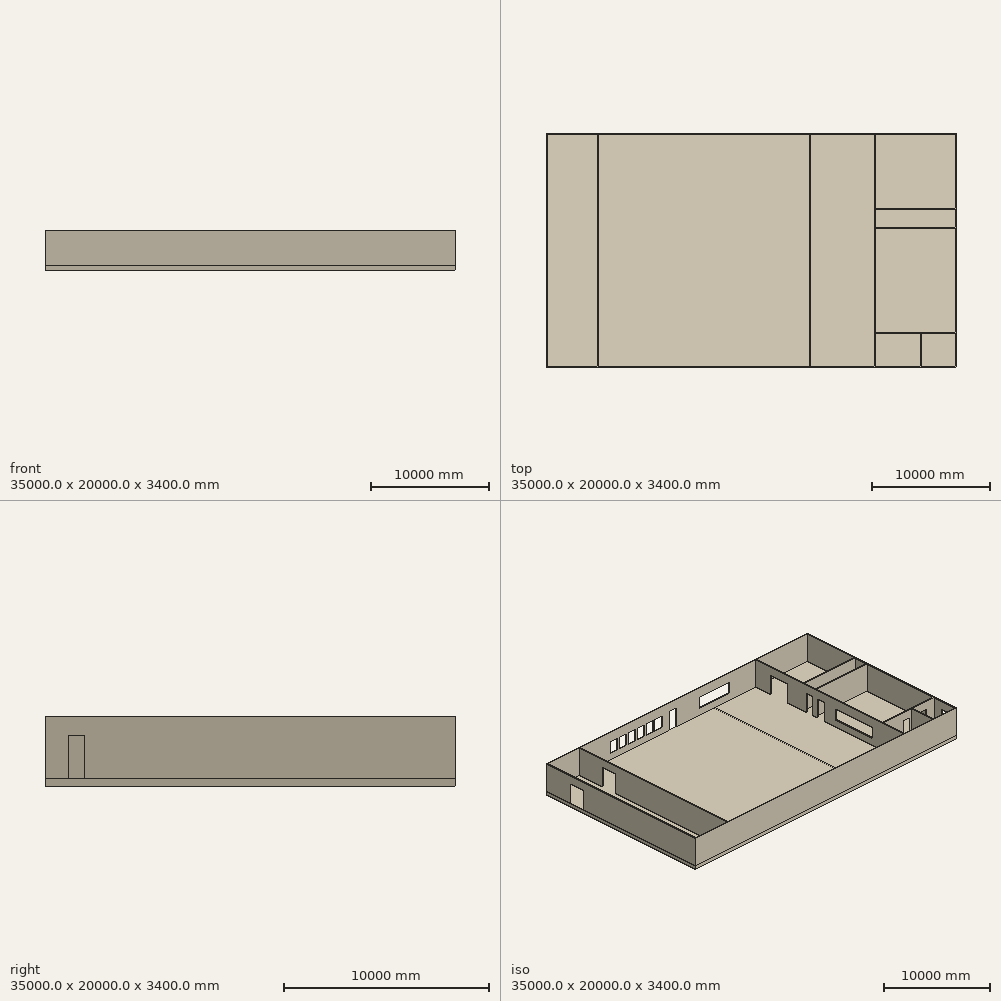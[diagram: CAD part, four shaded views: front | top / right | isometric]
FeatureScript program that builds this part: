
annotation { "Feature Type Name" : "Feature", "Feature Type Description" : "" }
export const myFeature = defineFeature(function(context is Context, id is Id, definition is map)
    precondition{}
    {
        {
            var Q0;
            Q0=qCreatedBy(makeId("Top.planeOp"),FACE);
            var sketch = newSketch(context, id + "F0", { "sketchPlane" : qUnion([Q0])});
            skLineSegment(sketch, "E0.bottom", {"start": v(0, 0) * mm, "end": v(-35000, 0) * mm});
            skLineSegment(sketch, "E0.right", {"start": v(-35000, 0) * mm, "end": v(-35000, 20000) * mm});
            skLineSegment(sketch, "E1.0", {"start": v(-34900, 100) * mm, "end": v(-34900, 19900) * mm});
            skLineSegment(sketch, "E2", {"start": v(-3000, 100) * mm, "end": v(-3000, 2905) * mm});
            skLineSegment(sketch, "E3", {"start": v(-3000, 2905) * mm, "end": v(-1985, 2905) * mm});
            skPoint(sketch, "E4", {"position": v(-100, 2905) * mm});
            skLineSegment(sketch, "E5", {"start": v(-1115, 2905) * mm, "end": v(-100, 2905) * mm});
            skLineSegment(sketch, "E6", {"start": v(-1985, 2905) * mm, "end": v(-1985, 3005) * mm});
            skLineSegment(sketch, "E7", {"start": v(-1115, 2905) * mm, "end": v(-1115, 3005) * mm});
            skLineSegment(sketch, "E8", {"start": v(-1115, 3005) * mm, "end": v(-100, 3005) * mm});
            skLineSegment(sketch, "E9", {"start": v(-3000, 100) * mm, "end": v(-100, 100) * mm});
            skLineSegment(sketch, "E10", {"start": v(-100, 2905) * mm, "end": v(-100, 1890) * mm});
            skLineSegment(sketch, "E11", {"start": v(-100, 100) * mm, "end": v(-100, 1115) * mm});
            skLineSegment(sketch, "E12", {"start": v(-100, 1115) * mm, "end": v(0, 1115) * mm});
            skLineSegment(sketch, "E13", {"start": v(0, 1115) * mm, "end": v(0, 0) * mm});
            skLineSegment(sketch, "E14", {"start": v(-100, 1890) * mm, "end": v(0, 1890) * mm});
            skLineSegment(sketch, "E15", {"start": v(0, 1890) * mm, "end": v(0, 20000) * mm});
            skLineSegment(sketch, "E16", {"start": v(0, 1890) * mm, "end": v(0, 1115) * mm});
            skLineSegment(sketch, "E17", {"start": v(-100, 11905) * mm, "end": v(-6900, 11905) * mm});
            skLineSegment(sketch, "E18", {"start": v(-6900, 12005) * mm, "end": v(-100, 12005) * mm});
            skLineSegment(sketch, "E19", {"start": v(-100, 3005) * mm, "end": v(-100, 11905) * mm});
            skLineSegment(sketch, "E20", {"start": v(-6900, 11905) * mm, "end": v(-6900, 11655) * mm});
            skLineSegment(sketch, "E21", {"start": v(-6900, 11655) * mm, "end": v(-7000, 11655) * mm});
            skLineSegment(sketch, "E22", {"start": v(-7000, 11655) * mm, "end": v(-7000, 12255) * mm});
            skLineSegment(sketch, "E23", {"start": v(-7000, 12255) * mm, "end": v(-6900, 12255) * mm});
            skLineSegment(sketch, "E24", {"start": v(-6900, 12255) * mm, "end": v(-6900, 12005) * mm});
            skLineSegment(sketch, "E25", {"start": v(-6900, 13125) * mm, "end": v(-7000, 13125) * mm});
            skLineSegment(sketch, "E26", {"start": v(-6900, 19900) * mm, "end": v(-95.24, 19900) * mm});
            skLineSegment(sketch, "E27", {"start": v(-3100, 100) * mm, "end": v(-6900, 100) * mm});
            skLineSegment(sketch, "E28", {"start": v(-7000, 100) * mm, "end": v(-7000, 10755) * mm});
            skLineSegment(sketch, "E29", {"start": v(-7000, 10755) * mm, "end": v(-6900, 10755) * mm});
            skLineSegment(sketch, "E30", {"start": v(-1985, 2905) * mm, "end": v(-1115, 2905) * mm});
            skLineSegment(sketch, "E31", {"start": v(-1985, 3005) * mm, "end": v(-1115, 3005) * mm});
            skLineSegment(sketch, "E32", {"start": v(-6900, 10755) * mm, "end": v(-6900, 11655) * mm});
            skLineSegment(sketch, "E33", {"start": v(-7000, 11655) * mm, "end": v(-7000, 10755) * mm});
            skLineSegment(sketch, "E34", {"start": v(-7000, 12255) * mm, "end": v(-7000, 13125) * mm});
            skLineSegment(sketch, "E35", {"start": v(-6900, 12255) * mm, "end": v(-6900, 13125) * mm});
            skLineSegment(sketch, "E36", {"start": v(-100, 1890) * mm, "end": v(-100, 1115) * mm});
            skLineSegment(sketch, "E37", {"start": v(-7000, 9255) * mm, "end": v(-6900, 9255) * mm});
            skLineSegment(sketch, "E38", {"start": v(-7000, 4255) * mm, "end": v(-6900, 4255) * mm});
            skLineSegment(sketch, "E39", {"start": v(-3100, 100) * mm, "end": v(-3100, 2905) * mm});
            skLineSegment(sketch, "E40", {"start": v(-6900, 100) * mm, "end": v(-6900, 2905) * mm});
            skLineSegment(sketch, "E41", {"start": v(-6900, 3005) * mm, "end": v(-6900, 9255) * mm});
            skLineSegment(sketch, "E42", {"start": v(-6900, 10755) * mm, "end": v(-6900, 9255) * mm});
            skLineSegment(sketch, "E43", {"start": v(-3100, 2905) * mm, "end": v(-3350, 2905) * mm});
            skLineSegment(sketch, "E44", {"start": v(-3350, 2905) * mm, "end": v(-4220, 2905) * mm});
            skLineSegment(sketch, "E45", {"start": v(-6900, 2905) * mm, "end": v(-4220, 2905) * mm});
            skLineSegment(sketch, "E46", {"start": v(-1985, 3005) * mm, "end": v(-3350, 3005) * mm});
            skLineSegment(sketch, "E47", {"start": v(-3350, 3005) * mm, "end": v(-4220, 3005) * mm});
            skLineSegment(sketch, "E48", {"start": v(-4220, 3005) * mm, "end": v(-6900, 3005) * mm});
            skLineSegment(sketch, "E49", {"start": v(-3350, 3005) * mm, "end": v(-3350, 2905) * mm});
            skLineSegment(sketch, "E50", {"start": v(-4220, 3005) * mm, "end": v(-4220, 2905) * mm});
            skLineSegment(sketch, "E51", {"start": v(-6900, 13505) * mm, "end": v(-100, 13505) * mm});
            skLineSegment(sketch, "E52", {"start": v(-6900, 13125) * mm, "end": v(-6900, 13505) * mm});
            skLineSegment(sketch, "E53", {"start": v(-100, 12005) * mm, "end": v(-100, 13505) * mm});
            skLineSegment(sketch, "E54", {"start": v(-95.24, 19900) * mm, "end": v(-95.24, 13605) * mm});
            skLineSegment(sketch, "E55", {"start": v(-95.24, 13605) * mm, "end": v(-6900, 13605) * mm});
            skLineSegment(sketch, "E56", {"start": v(-6900, 19900) * mm, "end": v(-6900, 17900) * mm});
            skLineSegment(sketch, "E57", {"start": v(-6900, 13605) * mm, "end": v(-6900, 15605) * mm});
            skLineSegment(sketch, "E58", {"start": v(-7000, 19900) * mm, "end": v(-7000, 17900) * mm});
            skLineSegment(sketch, "E59", {"start": v(-7000, 15605) * mm, "end": v(-7000, 13125) * mm});
            skLineSegment(sketch, "E60", {"start": v(-7000, 17900) * mm, "end": v(-6900, 17900) * mm});
            skLineSegment(sketch, "E61", {"start": v(-7000, 17900) * mm, "end": v(-7000, 15605) * mm});
            skLineSegment(sketch, "E62", {"start": v(-6900, 17900) * mm, "end": v(-6900, 15605) * mm});
            skLineSegment(sketch, "E63", {"start": v(-7000, 15605) * mm, "end": v(-6900, 15605) * mm});
            skLineSegment(sketch, "E64", {"start": v(-7000, 100) * mm, "end": v(-12500, 100) * mm});
            skLineSegment(sketch, "E65", {"start": v(-12500, 100) * mm, "end": v(-12500, 19900) * mm});
            skLineSegment(sketch, "E66", {"start": v(-12500, 19900) * mm, "end": v(-12550, 19900) * mm});
            skLineSegment(sketch, "E67", {"start": v(-12550, 19900) * mm, "end": v(-12550, 100) * mm});
            skLineSegment(sketch, "E68", {"start": v(-12500, 100) * mm, "end": v(-12550, 100) * mm});
            skLineSegment(sketch, "E69", {"start": v(-12550, 100) * mm, "end": v(-30550, 100) * mm});
            skLineSegment(sketch, "E70", {"start": v(-30550, 100) * mm, "end": v(-30550, 15100) * mm});
            skLineSegment(sketch, "E71", {"start": v(-30550, 15100) * mm, "end": v(-30550, 16840) * mm});
            skLineSegment(sketch, "E72", {"start": v(-30550, 16840) * mm, "end": v(-30550, 19900) * mm});
            skLineSegment(sketch, "E73", {"start": v(-7000, 19900) * mm, "end": v(-12500, 19900) * mm});
            skLineSegment(sketch, "E74", {"start": v(-34900, 100) * mm, "end": v(-30650, 100) * mm});
            skLineSegment(sketch, "E75", {"start": v(-30650, 100) * mm, "end": v(-30650, 15100) * mm});
            skLineSegment(sketch, "E76", {"start": v(-30650, 15100) * mm, "end": v(-30650, 16840) * mm});
            skLineSegment(sketch, "E77", {"start": v(-30650, 16840) * mm, "end": v(-30650, 19900) * mm});
            skLineSegment(sketch, "E78", {"start": v(-30650, 19900) * mm, "end": v(-34900, 19900) * mm});
            skLineSegment(sketch, "E79", {"start": v(-30650, 15100) * mm, "end": v(-30550, 15100) * mm});
            skLineSegment(sketch, "E80", {"start": v(-30650, 16840) * mm, "end": v(-30550, 16840) * mm});
            skLineSegment(sketch, "E81", {"start": v(-30550, 19900) * mm, "end": v(-26550, 19900) * mm});
            skLineSegment(sketch, "E82", {"start": v(-26550, 19900) * mm, "end": v(-25550, 19900) * mm});
            skLineSegment(sketch, "E83", {"start": v(-25550, 19900) * mm, "end": v(-25350, 19900) * mm});
            skLineSegment(sketch, "E84", {"start": v(-25350, 19900) * mm, "end": v(-24350, 19900) * mm});
            skLineSegment(sketch, "E85", {"start": v(-24350, 19900) * mm, "end": v(-24150, 19900) * mm});
            skLineSegment(sketch, "E86", {"start": v(-24150, 19900) * mm, "end": v(-23150, 19900) * mm});
            skLineSegment(sketch, "E87", {"start": v(-23150, 19900) * mm, "end": v(-22950, 19900) * mm});
            skLineSegment(sketch, "E88", {"start": v(-22950, 19900) * mm, "end": v(-21950, 19900) * mm});
            skLineSegment(sketch, "E89", {"start": v(-21950, 19900) * mm, "end": v(-21750, 19900) * mm});
            skLineSegment(sketch, "E90", {"start": v(-21750, 19900) * mm, "end": v(-20750, 19900) * mm});
            skLineSegment(sketch, "E91", {"start": v(-20750, 19900) * mm, "end": v(-20550, 19900) * mm});
            skLineSegment(sketch, "E92", {"start": v(-20550, 19900) * mm, "end": v(-19550, 19900) * mm});
            skLineSegment(sketch, "E93", {"start": v(-26550, 19900) * mm, "end": v(-26550, 20000) * mm});
            skLineSegment(sketch, "E94", {"start": v(-25550, 19900) * mm, "end": v(-25550, 20000) * mm});
            skLineSegment(sketch, "E95", {"start": v(-25350, 19900) * mm, "end": v(-25350, 20000) * mm});
            skLineSegment(sketch, "E96", {"start": v(-24350, 19900) * mm, "end": v(-24350, 20000) * mm});
            skLineSegment(sketch, "E97", {"start": v(-24150, 19900) * mm, "end": v(-24150, 20000) * mm});
            skLineSegment(sketch, "E98", {"start": v(-23150, 19900) * mm, "end": v(-23150, 20000) * mm});
            skLineSegment(sketch, "E99", {"start": v(-22950, 19900) * mm, "end": v(-22950, 20000) * mm});
            skLineSegment(sketch, "E100", {"start": v(-21950, 19900) * mm, "end": v(-21950, 20000) * mm});
            skLineSegment(sketch, "E101", {"start": v(-20750, 19900) * mm, "end": v(-20750, 20000) * mm});
            skLineSegment(sketch, "E102", {"start": v(-20550, 19900) * mm, "end": v(-20550, 20000) * mm});
            skLineSegment(sketch, "E103", {"start": v(-19550, 19900) * mm, "end": v(-19550, 20000) * mm});
            skLineSegment(sketch, "E104", {"start": v(-21750, 19900) * mm, "end": v(-21750, 20000) * mm});
            skLineSegment(sketch, "E105", {"start": v(-19550, 19900) * mm, "end": v(-18550, 19900) * mm});
            skLineSegment(sketch, "E106", {"start": v(-18550, 19900) * mm, "end": v(-17680, 19900) * mm});
            skLineSegment(sketch, "E107", {"start": v(-12550, 19900) * mm, "end": v(-17680, 19900) * mm});
            skLineSegment(sketch, "E108", {"start": v(-18550, 19900) * mm, "end": v(-18550, 20000) * mm});
            skLineSegment(sketch, "E109", {"start": v(-17680, 19900) * mm, "end": v(-17680, 20000) * mm});
            skLineSegment(sketch, "E110", {"start": v(0, 20000) * mm, "end": v(-17680, 20000) * mm});
            skLineSegment(sketch, "E111", {"start": v(-17680, 20000) * mm, "end": v(-18550, 20000) * mm});
            skLineSegment(sketch, "E112", {"start": v(-18550, 20000) * mm, "end": v(-19550, 20000) * mm});
            skLineSegment(sketch, "E113", {"start": v(-19550, 20000) * mm, "end": v(-20550, 20000) * mm});
            skLineSegment(sketch, "E114", {"start": v(-20550, 20000) * mm, "end": v(-20750, 20000) * mm});
            skLineSegment(sketch, "E115", {"start": v(-20750, 20000) * mm, "end": v(-21750, 20000) * mm});
            skLineSegment(sketch, "E116", {"start": v(-21750, 20000) * mm, "end": v(-21950, 20000) * mm});
            skLineSegment(sketch, "E117", {"start": v(-21950, 20000) * mm, "end": v(-22950, 20000) * mm});
            skLineSegment(sketch, "E118", {"start": v(-22950, 20000) * mm, "end": v(-23150, 20000) * mm});
            skLineSegment(sketch, "E119", {"start": v(-23150, 20000) * mm, "end": v(-24150, 20000) * mm});
            skLineSegment(sketch, "E120", {"start": v(-24150, 20000) * mm, "end": v(-24350, 20000) * mm});
            skLineSegment(sketch, "E121", {"start": v(-24350, 20000) * mm, "end": v(-25350, 20000) * mm});
            skLineSegment(sketch, "E122", {"start": v(-25350, 20000) * mm, "end": v(-25550, 20000) * mm});
            skLineSegment(sketch, "E123", {"start": v(-25550, 20000) * mm, "end": v(-26550, 20000) * mm});
            skLineSegment(sketch, "E124", {"start": v(-26550, 20000) * mm, "end": v(-35000, 20000) * mm});
            skLineSegment(sketch, "E125", {"start": v(-35000, 15100) * mm, "end": v(-34900, 15100) * mm});
            skLineSegment(sketch, "E126", {"start": v(-35000, 16840) * mm, "end": v(-34900, 16840) * mm});
            skLineSegment(sketch, "E127", {"start": v(-14600, 20000) * mm, "end": v(-14600, 19900) * mm});
            skLineSegment(sketch, "E128", {"start": v(-10600, 20000) * mm, "end": v(-10600, 19900) * mm});
            skSolve(sketch);
        }
        {
            var Q0;
            Q0=makeQuery(id+"F0.imprint","IMPRINT",FACE,{"disambiguationData":[TD([[makeQuery(id+"F0.imprint","IMPRINT",EDGE,{"derivedFrom":sQuery(id+"F0.wireOp",EDGE,"E1.0")}),-1.0]])]});
            var Q1;
            Q1=makeQuery(id+"F0.imprint","IMPRINT",FACE,{"disambiguationData":[TD([[makeQuery(id+"F0.imprint","IMPRINT",EDGE,{"derivedFrom":sQuery(id+"F0.wireOp",EDGE,"E0.bottom")}),-1.0]])]});
            var Q2;
            Q2=makeQuery(id+"F0.imprint","IMPRINT",FACE,{"disambiguationData":[TD([[makeQuery(id+"F0.imprint","IMPRINT",EDGE,{"derivedFrom":sQuery(id+"F0.wireOp",EDGE,"E2")}),-1.0]])]});
            var Q3;
            Q3=makeQuery(id+"F0.imprint","IMPRINT",FACE,{"disambiguationData":[TD([[makeQuery(id+"F0.imprint","IMPRINT",EDGE,{"derivedFrom":sQuery(id+"F0.wireOp",EDGE,"E12")}),1.0]])]});
            var Q4;
            Q4=makeQuery(id+"F0.imprint","IMPRINT",FACE,{"disambiguationData":[TD([[makeQuery(id+"F0.imprint","IMPRINT",EDGE,{"derivedFrom":sQuery(id+"F0.wireOp",EDGE,"E6")}),-1.0]])]});
            var Q5;
            Q5=makeQuery(id+"F0.imprint","IMPRINT",FACE,{"disambiguationData":[TD([[makeQuery(id+"F0.imprint","IMPRINT",EDGE,{"derivedFrom":sQuery(id+"F0.wireOp",EDGE,"6b3fb178-0d36-4cbd-b119-71aa7d92e045.4")}),1.0]])]});
            var Q6;
            Q6=makeQuery(id+"F0.imprint","IMPRINT",FACE,{"disambiguationData":[TD([[makeQuery(id+"F0.imprint","IMPRINT",EDGE,{"derivedFrom":sQuery(id+"F0.wireOp",EDGE,"E21")}),1.0]])]});
            var Q7;
            Q7=makeQuery(id+"F0.imprint","IMPRINT",FACE,{"disambiguationData":[TD([[makeQuery(id+"F0.imprint","IMPRINT",EDGE,{"derivedFrom":sQuery(id+"F0.wireOp",EDGE,"E18")}),1.0]])]});
            var Q8;
            Q8=makeQuery(id+"F0.imprint","IMPRINT",FACE,{"disambiguationData":[TD([[makeQuery(id+"F0.imprint","IMPRINT",EDGE,{"derivedFrom":sQuery(id+"F0.wireOp",EDGE,"E23")}),1.0]])]});
            var Q9;
            {var subQ0=sQuery(id+"F0.wireOp",EDGE,"E37");Q9=makeQuery(id+"F0.imprint","IMPRINT",FACE,{"disambiguationData":[TD([[makeQuery(id+"F0.imprint","IMPRINT",EDGE,{"derivedFrom":subQ0}),-1.0]])]});}
            var Q10;
            {var subQ0=sQuery(id+"F0.wireOp",EDGE,"E29");Q10=makeQuery(id+"F0.imprint","IMPRINT",FACE,{"disambiguationData":[TD([[makeQuery(id+"F0.imprint","IMPRINT",EDGE,{"derivedFrom":subQ0}),-1.0]])]});}
            var Q11;
            {var subQ5=sQuery(id+"F0.wireOp",EDGE,"KWLxwDUW-hbxq-1viL-1m08-Hg8gEenvGZlB");Q11=makeQuery(id+"F0.imprint","IMPRINT",FACE,{"disambiguationData":[TD([[makeQuery(id+"F0.imprint","IMPRINT",EDGE,{"derivedFrom":subQ5}),-1.0]])]});}
            var Q12;
            {var subQ0=sQuery(id+"F0.wireOp",EDGE,"sINUJQdt-DprZ-GAcK-VXLo-GtyemsUMvXYI");Q12=makeQuery(id+"F0.imprint","IMPRINT",FACE,{"disambiguationData":[TD([[makeQuery(id+"F0.imprint","IMPRINT",EDGE,{"derivedFrom":subQ0}),-1.0]])]});}
            var Q13;
            Q13=makeQuery(id+"F0.imprint","IMPRINT",FACE,{"disambiguationData":[TD([[makeQuery(id+"F0.imprint","IMPRINT",EDGE,{"derivedFrom":sQuery(id+"F0.wireOp",EDGE,"E27")}),-1.0]])]});
            var Q14;
            Q14=makeQuery(id+"F0.imprint","IMPRINT",FACE,{"disambiguationData":[TD([[makeQuery(id+"F0.imprint","IMPRINT",EDGE,{"derivedFrom":sQuery(id+"F0.wireOp",EDGE,"E8")}),1.0]])]});
            var Q15;
            Q15=makeQuery(id+"F0.imprint","IMPRINT",FACE,{"disambiguationData":[TD([[makeQuery(id+"F0.imprint","IMPRINT",EDGE,{"derivedFrom":sQuery(id+"F0.wireOp",EDGE,"E44")}),-1.0]])]});
            var Q16;
            Q16=makeQuery(id+"F0.imprint","IMPRINT",FACE,{"disambiguationData":[TD([[makeQuery(id+"F0.imprint","IMPRINT",EDGE,{"derivedFrom":sQuery(id+"F0.wireOp",EDGE,"E26")}),-1.0]])]});
            var Q17;
            Q17=makeQuery(id+"F0.imprint","IMPRINT",FACE,{"disambiguationData":[TD([[makeQuery(id+"F0.imprint","IMPRINT",EDGE,{"derivedFrom":sQuery(id+"F0.wireOp",EDGE,"E60")}),-1.0]])]});
            var Q18;
            Q18=makeQuery(id+"F0.imprint","IMPRINT",FACE,{"disambiguationData":[TD([[makeQuery(id+"F0.imprint","IMPRINT",EDGE,{"derivedFrom":sQuery(id+"F0.wireOp",EDGE,"E67")}),-1.0]])]});
            var Q19;
            Q19=makeQuery(id+"F0.imprint","IMPRINT",FACE,{"disambiguationData":[TD([[makeQuery(id+"F0.imprint","IMPRINT",EDGE,{"derivedFrom":sQuery(id+"F0.wireOp",EDGE,"E22")}),1.0]])]});
            var Q20;
            Q20=makeQuery(id+"F0.imprint","IMPRINT",FACE,{"disambiguationData":[TD([[makeQuery(id+"F0.imprint","IMPRINT",EDGE,{"derivedFrom":sQuery(id+"F0.wireOp",EDGE,"E65")}),1.0]])]});
            var Q21;
            Q21=makeQuery(id+"F0.imprint","IMPRINT",FACE,{"disambiguationData":[TD([[makeQuery(id+"F0.imprint","IMPRINT",EDGE,{"derivedFrom":sQuery(id+"F0.wireOp",EDGE,"E71")}),1.0]])]});
            var Q22;
            Q22=makeQuery(id+"F0.imprint","IMPRINT",FACE,{"disambiguationData":[TD([[makeQuery(id+"F0.imprint","IMPRINT",EDGE,{"derivedFrom":sQuery(id+"F0.wireOp",EDGE,"E82")}),1.0]])]});
            var Q23;
            Q23=makeQuery(id+"F0.imprint","IMPRINT",FACE,{"disambiguationData":[TD([[makeQuery(id+"F0.imprint","IMPRINT",EDGE,{"derivedFrom":sQuery(id+"F0.wireOp",EDGE,"E83")}),1.0]])]});
            var Q24;
            Q24=makeQuery(id+"F0.imprint","IMPRINT",FACE,{"disambiguationData":[TD([[makeQuery(id+"F0.imprint","IMPRINT",EDGE,{"derivedFrom":sQuery(id+"F0.wireOp",EDGE,"E84")}),1.0]])]});
            var Q25;
            Q25=makeQuery(id+"F0.imprint","IMPRINT",FACE,{"disambiguationData":[TD([[makeQuery(id+"F0.imprint","IMPRINT",EDGE,{"derivedFrom":sQuery(id+"F0.wireOp",EDGE,"E85")}),1.0]])]});
            var Q26;
            Q26=makeQuery(id+"F0.imprint","IMPRINT",FACE,{"disambiguationData":[TD([[makeQuery(id+"F0.imprint","IMPRINT",EDGE,{"derivedFrom":sQuery(id+"F0.wireOp",EDGE,"E86")}),1.0]])]});
            var Q27;
            Q27=makeQuery(id+"F0.imprint","IMPRINT",FACE,{"disambiguationData":[TD([[makeQuery(id+"F0.imprint","IMPRINT",EDGE,{"derivedFrom":sQuery(id+"F0.wireOp",EDGE,"E87")}),1.0]])]});
            var Q28;
            Q28=makeQuery(id+"F0.imprint","IMPRINT",FACE,{"disambiguationData":[TD([[makeQuery(id+"F0.imprint","IMPRINT",EDGE,{"derivedFrom":sQuery(id+"F0.wireOp",EDGE,"E88")}),1.0]])]});
            var Q29;
            Q29=makeQuery(id+"F0.imprint","IMPRINT",FACE,{"disambiguationData":[TD([[makeQuery(id+"F0.imprint","IMPRINT",EDGE,{"derivedFrom":sQuery(id+"F0.wireOp",EDGE,"E89")}),1.0]])]});
            var Q30;
            Q30=makeQuery(id+"F0.imprint","IMPRINT",FACE,{"disambiguationData":[TD([[makeQuery(id+"F0.imprint","IMPRINT",EDGE,{"derivedFrom":sQuery(id+"F0.wireOp",EDGE,"E90")}),1.0]])]});
            var Q31;
            Q31=makeQuery(id+"F0.imprint","IMPRINT",FACE,{"disambiguationData":[TD([[makeQuery(id+"F0.imprint","IMPRINT",EDGE,{"derivedFrom":sQuery(id+"F0.wireOp",EDGE,"E91")}),1.0]])]});
            var Q32;
            Q32=makeQuery(id+"F0.imprint","IMPRINT",FACE,{"disambiguationData":[TD([[makeQuery(id+"F0.imprint","IMPRINT",EDGE,{"derivedFrom":sQuery(id+"F0.wireOp",EDGE,"E92")}),1.0]])]});
            var Q33;
            Q33=makeQuery(id+"F0.imprint","IMPRINT",FACE,{"disambiguationData":[TD([[makeQuery(id+"F0.imprint","IMPRINT",EDGE,{"derivedFrom":sQuery(id+"F0.wireOp",EDGE,"E103")}),-1.0]])]});
            var Q34;
            Q34=makeQuery(id+"F0.imprint","IMPRINT",FACE,{"disambiguationData":[TD([[makeQuery(id+"F0.imprint","IMPRINT",EDGE,{"derivedFrom":sQuery(id+"F0.wireOp",EDGE,"E106")}),1.0]])]});
            var Q35;
            Q35=makeQuery(id+"F0.imprint","IMPRINT",FACE,{"disambiguationData":[TD([[makeQuery(id+"F0.imprint","IMPRINT",EDGE,{"derivedFrom":sQuery(id+"F0.wireOp",EDGE,"E5")}),1.0]])]});
            var Q36;
            Q36=makeQuery(id+"F0.imprint","IMPRINT",FACE,{"disambiguationData":[TD([[makeQuery(id+"F0.imprint","IMPRINT",EDGE,{"derivedFrom":sQuery(id+"F0.wireOp",EDGE,"E72")}),1.0]])]});
            var Q37;
            {var subQ0=sQuery(id+"F0.wireOp",EDGE,"E125");Q37=makeQuery(id+"F0.imprint","IMPRINT",FACE,{"disambiguationData":[TD([[makeQuery(id+"F0.imprint","IMPRINT",EDGE,{"derivedFrom":subQ0}),1.0]])]});}
            var Q38;
            {var subQ4=sQuery(id+"F0.wireOp",EDGE,"E66");Q38=makeQuery(id+"F0.imprint","IMPRINT",FACE,{"disambiguationData":[TD([[makeQuery(id+"F0.imprint","IMPRINT",EDGE,{"derivedFrom":subQ4}),-1.0]])]});}
            var Q39;
            {var subQ0=sQuery(id+"F0.wireOp",EDGE,"E109");Q39=makeQuery(id+"F0.imprint","IMPRINT",FACE,{"disambiguationData":[TD([[makeQuery(id+"F0.imprint","IMPRINT",EDGE,{"derivedFrom":subQ0}),-1.0]])]});}
            extrude(context, id + "F1", {"entities" : qUnion([Q0, Q1, Q2, Q3, Q4, Q5, Q6, Q7, Q8, Q9, Q10, Q11, Q12, Q13, Q14, Q15, Q16, Q17, Q18, Q19, Q20, Q21, Q22, Q23, Q24, Q25, Q26, Q27, Q28, Q29, Q30, Q31, Q32, Q33, Q34, Q35, Q36, Q37, Q38, Q39]), "oppositeDirection" : true, "depth" : 400 * mm, "offsetDistance" : 25 * mm});
        }
        {
            var Q0;
            Q0=makeQuery(id+"F0.imprint","IMPRINT",FACE,{"disambiguationData":[TD([[makeQuery(id+"F0.imprint","IMPRINT",EDGE,{"derivedFrom":sQuery(id+"F0.wireOp",EDGE,"E0.bottom")}),-1.0]])]});
            var Q1;
            Q1=makeQuery(id+"F0.imprint","IMPRINT",FACE,{"disambiguationData":[TD([[makeQuery(id+"F0.imprint","IMPRINT",EDGE,{"derivedFrom":sQuery(id+"F0.wireOp",EDGE,"E6")}),-1.0]])]});
            var Q2;
            Q2=makeQuery(id+"F0.imprint","IMPRINT",FACE,{"disambiguationData":[TD([[makeQuery(id+"F0.imprint","IMPRINT",EDGE,{"derivedFrom":sQuery(id+"F0.wireOp",EDGE,"E12")}),1.0]])]});
            var Q3;
            Q3=makeQuery(id+"F0.imprint","IMPRINT",FACE,{"disambiguationData":[TD([[makeQuery(id+"F0.imprint","IMPRINT",EDGE,{"derivedFrom":sQuery(id+"F0.wireOp",EDGE,"E23")}),1.0]])]});
            var Q4;
            Q4=makeQuery(id+"F0.imprint","IMPRINT",FACE,{"disambiguationData":[TD([[makeQuery(id+"F0.imprint","IMPRINT",EDGE,{"derivedFrom":sQuery(id+"F0.wireOp",EDGE,"E21")}),1.0]])]});
            var Q5;
            {var subQ0=sQuery(id+"F0.wireOp",EDGE,"E37");Q5=makeQuery(id+"F0.imprint","IMPRINT",FACE,{"disambiguationData":[TD([[makeQuery(id+"F0.imprint","IMPRINT",EDGE,{"derivedFrom":subQ0}),-1.0]])]});}
            var Q6;
            {var subQ0=sQuery(id+"F0.wireOp",EDGE,"E29");Q6=makeQuery(id+"F0.imprint","IMPRINT",FACE,{"disambiguationData":[TD([[makeQuery(id+"F0.imprint","IMPRINT",EDGE,{"derivedFrom":subQ0}),-1.0]])]});}
            var Q7;
            Q7=makeQuery(id+"F0.imprint","IMPRINT",FACE,{"disambiguationData":[TD([[makeQuery(id+"F0.imprint","IMPRINT",EDGE,{"derivedFrom":sQuery(id+"F0.wireOp",EDGE,"sINUJQdt-DprZ-GAcK-VXLo-GtyemsUMvXYI")}),-1.0]])]});
            var Q8;
            Q8=makeQuery(id+"F0.imprint","IMPRINT",FACE,{"disambiguationData":[TD([[makeQuery(id+"F0.imprint","IMPRINT",EDGE,{"derivedFrom":sQuery(id+"F0.wireOp",EDGE,"E44")}),-1.0]])]});
            var Q9;
            Q9=makeQuery(id+"F0.imprint","IMPRINT",FACE,{"disambiguationData":[TD([[makeQuery(id+"F0.imprint","IMPRINT",EDGE,{"derivedFrom":sQuery(id+"F0.wireOp",EDGE,"rL4nEPrz-xR3R-JLyK-HAKY-g2uvk8zqw2Dq")}),1.0]])]});
            var Q10;
            Q10=makeQuery(id+"F0.imprint","IMPRINT",FACE,{"disambiguationData":[TD([[makeQuery(id+"F0.imprint","IMPRINT",EDGE,{"derivedFrom":sQuery(id+"F0.wireOp",EDGE,"E60")}),-1.0]])]});
            var Q11;
            Q11=makeQuery(id+"F0.imprint","IMPRINT",FACE,{"disambiguationData":[TD([[makeQuery(id+"F0.imprint","IMPRINT",EDGE,{"derivedFrom":sQuery(id+"F0.wireOp",EDGE,"E71")}),1.0]])]});
            var Q12;
            Q12=makeQuery(id+"F0.imprint","IMPRINT",FACE,{"disambiguationData":[TD([[makeQuery(id+"F0.imprint","IMPRINT",EDGE,{"derivedFrom":sQuery(id+"F0.wireOp",EDGE,"E5")}),1.0]])]});
            var Q13;
            Q13=makeQuery(id+"F0.imprint","IMPRINT",FACE,{"disambiguationData":[TD([[makeQuery(id+"F0.imprint","IMPRINT",EDGE,{"derivedFrom":sQuery(id+"F0.wireOp",EDGE,"E82")}),1.0]])]});
            var Q14;
            Q14=makeQuery(id+"F0.imprint","IMPRINT",FACE,{"disambiguationData":[TD([[makeQuery(id+"F0.imprint","IMPRINT",EDGE,{"derivedFrom":sQuery(id+"F0.wireOp",EDGE,"E83")}),1.0]])]});
            var Q15;
            Q15=makeQuery(id+"F0.imprint","IMPRINT",FACE,{"disambiguationData":[TD([[makeQuery(id+"F0.imprint","IMPRINT",EDGE,{"derivedFrom":sQuery(id+"F0.wireOp",EDGE,"E84")}),1.0]])]});
            var Q16;
            Q16=makeQuery(id+"F0.imprint","IMPRINT",FACE,{"disambiguationData":[TD([[makeQuery(id+"F0.imprint","IMPRINT",EDGE,{"derivedFrom":sQuery(id+"F0.wireOp",EDGE,"E85")}),1.0]])]});
            var Q17;
            Q17=makeQuery(id+"F0.imprint","IMPRINT",FACE,{"disambiguationData":[TD([[makeQuery(id+"F0.imprint","IMPRINT",EDGE,{"derivedFrom":sQuery(id+"F0.wireOp",EDGE,"E86")}),1.0]])]});
            var Q18;
            Q18=makeQuery(id+"F0.imprint","IMPRINT",FACE,{"disambiguationData":[TD([[makeQuery(id+"F0.imprint","IMPRINT",EDGE,{"derivedFrom":sQuery(id+"F0.wireOp",EDGE,"E87")}),1.0]])]});
            var Q19;
            Q19=makeQuery(id+"F0.imprint","IMPRINT",FACE,{"disambiguationData":[TD([[makeQuery(id+"F0.imprint","IMPRINT",EDGE,{"derivedFrom":sQuery(id+"F0.wireOp",EDGE,"E88")}),1.0]])]});
            var Q20;
            Q20=makeQuery(id+"F0.imprint","IMPRINT",FACE,{"disambiguationData":[TD([[makeQuery(id+"F0.imprint","IMPRINT",EDGE,{"derivedFrom":sQuery(id+"F0.wireOp",EDGE,"E89")}),1.0]])]});
            var Q21;
            Q21=makeQuery(id+"F0.imprint","IMPRINT",FACE,{"disambiguationData":[TD([[makeQuery(id+"F0.imprint","IMPRINT",EDGE,{"derivedFrom":sQuery(id+"F0.wireOp",EDGE,"E90")}),1.0]])]});
            var Q22;
            Q22=makeQuery(id+"F0.imprint","IMPRINT",FACE,{"disambiguationData":[TD([[makeQuery(id+"F0.imprint","IMPRINT",EDGE,{"derivedFrom":sQuery(id+"F0.wireOp",EDGE,"E91")}),1.0]])]});
            var Q23;
            Q23=makeQuery(id+"F0.imprint","IMPRINT",FACE,{"disambiguationData":[TD([[makeQuery(id+"F0.imprint","IMPRINT",EDGE,{"derivedFrom":sQuery(id+"F0.wireOp",EDGE,"E92")}),1.0]])]});
            var Q24;
            Q24=makeQuery(id+"F0.imprint","IMPRINT",FACE,{"disambiguationData":[TD([[makeQuery(id+"F0.imprint","IMPRINT",EDGE,{"derivedFrom":sQuery(id+"F0.wireOp",EDGE,"E103")}),-1.0]])]});
            var Q25;
            Q25=makeQuery(id+"F0.imprint","IMPRINT",FACE,{"disambiguationData":[TD([[makeQuery(id+"F0.imprint","IMPRINT",EDGE,{"derivedFrom":sQuery(id+"F0.wireOp",EDGE,"E106")}),1.0]])]});
            var Q26;
            {var subQ0=sQuery(id+"F0.wireOp",EDGE,"E125");Q26=makeQuery(id+"F0.imprint","IMPRINT",FACE,{"disambiguationData":[TD([[makeQuery(id+"F0.imprint","IMPRINT",EDGE,{"derivedFrom":subQ0}),1.0]])]});}
            var Q27;
            Q27=makeQuery(id+"F0.imprint","IMPRINT",FACE,{"disambiguationData":[TD([[makeQuery(id+"F0.imprint","IMPRINT",EDGE,{"derivedFrom":sQuery(id+"F0.wireOp",EDGE,"E72")}),1.0]])]});
            var Q28;
            {var subQ4=sQuery(id+"F0.wireOp",EDGE,"E66");Q28=makeQuery(id+"F0.imprint","IMPRINT",FACE,{"disambiguationData":[TD([[makeQuery(id+"F0.imprint","IMPRINT",EDGE,{"derivedFrom":subQ4}),-1.0]])]});}
            var Q29;
            {var subQ0=sQuery(id+"F0.wireOp",EDGE,"E109");Q29=makeQuery(id+"F0.imprint","IMPRINT",FACE,{"disambiguationData":[TD([[makeQuery(id+"F0.imprint","IMPRINT",EDGE,{"derivedFrom":subQ0}),-1.0]])]});}
            extrude(context, id + "F2", {"entities" : qUnion([Q0, Q1, Q2, Q3, Q4, Q5, Q6, Q7, Q8, Q9, Q10, Q11, Q12, Q13, Q14, Q15, Q16, Q17, Q18, Q19, Q20, Q21, Q22, Q23, Q24, Q25, Q26, Q27, Q28, Q29]), "depth" : 3000 * mm, "offsetDistance" : 25 * mm});
        }
        {
            var Q0;
            Q0=makeQuery(id+"F0.imprint","IMPRINT",FACE,{"disambiguationData":[TD([[makeQuery(id+"F0.imprint","IMPRINT",EDGE,{"derivedFrom":sQuery(id+"F0.wireOp",EDGE,"E23")}),1.0]])]});
            var Q1;
            Q1=makeQuery(id+"F0.imprint","IMPRINT",FACE,{"disambiguationData":[TD([[makeQuery(id+"F0.imprint","IMPRINT",EDGE,{"derivedFrom":sQuery(id+"F0.wireOp",EDGE,"E21")}),1.0]])]});
            var Q2;
            Q2=makeQuery(id+"F0.imprint","IMPRINT",FACE,{"disambiguationData":[TD([[makeQuery(id+"F0.imprint","IMPRINT",EDGE,{"derivedFrom":sQuery(id+"F0.wireOp",EDGE,"E12")}),1.0]])]});
            var Q3;
            Q3=makeQuery(id+"F0.imprint","IMPRINT",FACE,{"disambiguationData":[TD([[makeQuery(id+"F0.imprint","IMPRINT",EDGE,{"derivedFrom":sQuery(id+"F0.wireOp",EDGE,"E6")}),-1.0]])]});
            var Q4;
            Q4=makeQuery(id+"F0.imprint","IMPRINT",FACE,{"disambiguationData":[TD([[makeQuery(id+"F0.imprint","IMPRINT",EDGE,{"derivedFrom":sQuery(id+"F0.wireOp",EDGE,"E44")}),-1.0]])]});
            var Q5;
            Q5=makeQuery(id+"F0.imprint","IMPRINT",FACE,{"disambiguationData":[TD([[makeQuery(id+"F0.imprint","IMPRINT",EDGE,{"derivedFrom":sQuery(id+"F0.wireOp",EDGE,"E60")}),-1.0]])]});
            var Q6;
            Q6=makeQuery(id+"F0.imprint","IMPRINT",FACE,{"disambiguationData":[TD([[makeQuery(id+"F0.imprint","IMPRINT",EDGE,{"derivedFrom":sQuery(id+"F0.wireOp",EDGE,"E71")}),1.0]])]});
            var Q7;
            Q7=makeQuery(id+"F0.imprint","IMPRINT",FACE,{"disambiguationData":[TD([[makeQuery(id+"F0.imprint","IMPRINT",EDGE,{"derivedFrom":sQuery(id+"F0.wireOp",EDGE,"E106")}),1.0]])]});
            var Q8;
            {var subQ0=sQuery(id+"F0.wireOp",EDGE,"E125");Q8=makeQuery(id+"F0.imprint","IMPRINT",FACE,{"disambiguationData":[TD([[makeQuery(id+"F0.imprint","IMPRINT",EDGE,{"derivedFrom":subQ0}),1.0]])]});}
            extrude(context, id + "F3", {"entities" : qUnion([Q0, Q1, Q2, Q3, Q4, Q5, Q6, Q7, Q8]), "operationType" : NewBodyOperationType.REMOVE, "oppositeDirection" : true, "depth" : 0 * mm, "offsetDistance" : 25 * mm, "hasSecondDirection" : true, "secondDirectionOppositeDirection" : false, "secondDirectionDepth" : 2100 * mm});
        }
        {
            var Q0;
            {var subQ0=sQuery(id+"F0.wireOp",EDGE,"E37");Q0=makeQuery(id+"F0.imprint","IMPRINT",FACE,{"disambiguationData":[TD([[makeQuery(id+"F0.imprint","IMPRINT",EDGE,{"derivedFrom":subQ0}),-1.0]])]});}
            var Q1;
            {var subQ4=sQuery(id+"F0.wireOp",EDGE,"E66");Q1=makeQuery(id+"F0.imprint","IMPRINT",FACE,{"disambiguationData":[TD([[makeQuery(id+"F0.imprint","IMPRINT",EDGE,{"derivedFrom":subQ4}),-1.0]])]});}
            extrude(context, id + "F4", {"entities" : qUnion([Q0, Q1]), "operationType" : NewBodyOperationType.REMOVE, "endBound" : BoundingType.UP_TO_NEXT, "depth" : 25 * mm, "hasOffset" : true, "offsetDistance" : 1000 * mm, "hasSecondDirection" : true, "secondDirectionOppositeDirection" : false, "secondDirectionDepth" : 800 * mm});
        }
        {
            var Q0;
            Q0=makeQuery(id+"F0.imprint","IMPRINT",FACE,{"disambiguationData":[TD([[makeQuery(id+"F0.imprint","IMPRINT",EDGE,{"derivedFrom":sQuery(id+"F0.wireOp",EDGE,"E82")}),1.0]])]});
            var Q1;
            Q1=makeQuery(id+"F0.imprint","IMPRINT",FACE,{"disambiguationData":[TD([[makeQuery(id+"F0.imprint","IMPRINT",EDGE,{"derivedFrom":sQuery(id+"F0.wireOp",EDGE,"E84")}),1.0]])]});
            var Q2;
            Q2=makeQuery(id+"F0.imprint","IMPRINT",FACE,{"disambiguationData":[TD([[makeQuery(id+"F0.imprint","IMPRINT",EDGE,{"derivedFrom":sQuery(id+"F0.wireOp",EDGE,"E86")}),1.0]])]});
            var Q3;
            Q3=makeQuery(id+"F0.imprint","IMPRINT",FACE,{"disambiguationData":[TD([[makeQuery(id+"F0.imprint","IMPRINT",EDGE,{"derivedFrom":sQuery(id+"F0.wireOp",EDGE,"E88")}),1.0]])]});
            var Q4;
            Q4=makeQuery(id+"F0.imprint","IMPRINT",FACE,{"disambiguationData":[TD([[makeQuery(id+"F0.imprint","IMPRINT",EDGE,{"derivedFrom":sQuery(id+"F0.wireOp",EDGE,"E90")}),1.0]])]});
            var Q5;
            Q5=makeQuery(id+"F0.imprint","IMPRINT",FACE,{"disambiguationData":[TD([[makeQuery(id+"F0.imprint","IMPRINT",EDGE,{"derivedFrom":sQuery(id+"F0.wireOp",EDGE,"E92")}),1.0]])]});
            extrude(context, id + "F5", {"entities" : qUnion([Q0, Q1, Q2, Q3, Q4, Q5]), "operationType" : NewBodyOperationType.REMOVE, "endBound" : BoundingType.UP_TO_NEXT, "depth" : 25 * mm, "hasOffset" : true, "offsetDistance" : 1000 * mm, "hasSecondDirection" : true, "secondDirectionOppositeDirection" : false, "secondDirectionDepth" : 700 * mm});
        }
        {
            var Q0;
            Q0=makeQuery(id+"F0.imprint","IMPRINT",FACE,{"disambiguationData":[TD([[makeQuery(id+"F0.imprint","IMPRINT",EDGE,{"derivedFrom":sQuery(id+"F0.wireOp",EDGE,"E65")}),1.0]])]});
            extrude(context, id + "F6", {"entities" : qUnion([Q0]), "depth" : 25 * mm, "offsetDistance" : 25 * mm});
        }
    });
